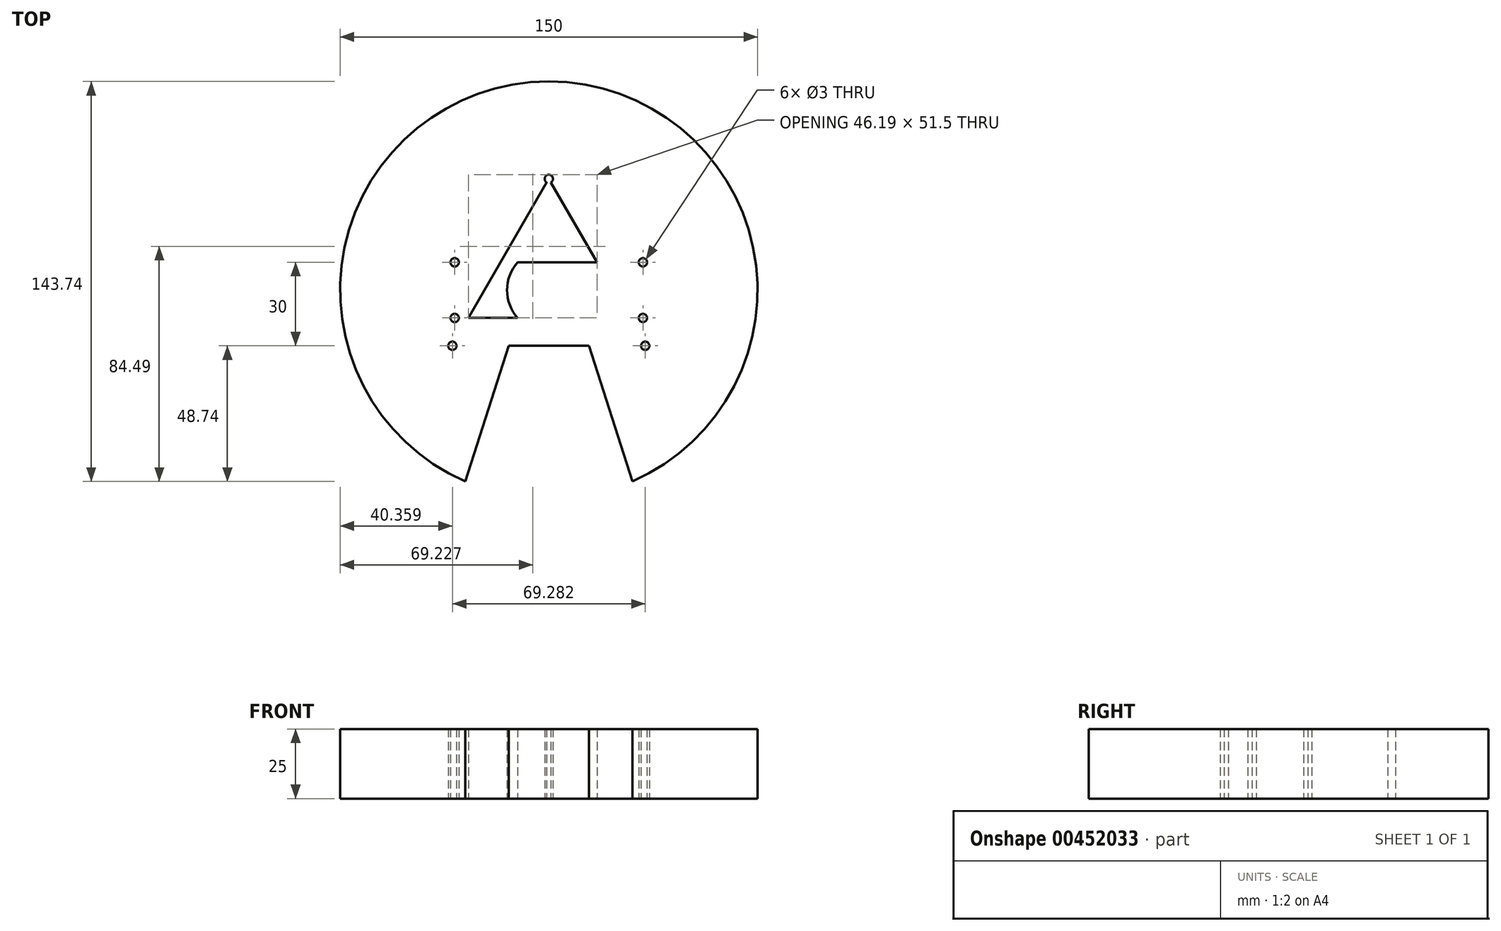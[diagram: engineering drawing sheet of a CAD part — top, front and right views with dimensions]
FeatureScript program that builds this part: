
annotation { "Feature Type Name" : "Feature", "Feature Type Description" : "" }
export const myFeature = defineFeature(function(context is Context, id is Id, definition is map)
    precondition{}
    {
        {
            var Q0;
            Q0=qCreatedBy(makeId("Top.planeOp"),FACE);
            var sketch = newSketch(context, id + "F0", { "sketchPlane" : qUnion([Q0])});
            skCircle(sketch, "E0", {"center": v(0, 0) * mm, "radius": 75 * mm});
            skCircle(sketch, "E1", {"center": v(0, 0) * mm, "radius": 15 * mm});
            skLineSegment(sketch, "E2.bottom", {"start": v(33.82, -10) * mm, "end": v(-33.82, -10) * mm});
            skLineSegment(sketch, "E2.top", {"start": v(33.82, 10) * mm, "end": v(-33.82, 10) * mm});
            skLineSegment(sketch, "E2.left", {"start": v(33.82, -10) * mm, "end": v(33.82, 10) * mm});
            skLineSegment(sketch, "E2.right", {"start": v(-33.82, -10) * mm, "end": v(-33.82, 10) * mm});
            skCircle(sketch, "E3.cCircle", {"center": v(0, 0) * mm, "radius": 20 * mm, "construction": true});
            skLineSegment(sketch, "E3.0", {"start": v(34.64, -20) * mm, "end": v(-34.64, -20) * mm});
            skLineSegment(sketch, "E3.1", {"start": v(-34.64, -20) * mm, "end": v(0, 40) * mm});
            skLineSegment(sketch, "E3.2", {"start": v(0, 40) * mm, "end": v(34.64, -20) * mm});
            skPoint(sketch, "E3.0.midPoint", {"position": v(0, -20) * mm});
            skCircle(sketch, "E4", {"center": v(0, 40) * mm, "radius": 1.5 * mm});
            skCircle(sketch, "E5", {"center": v(34.64, -20) * mm, "radius": 1.5 * mm});
            skCircle(sketch, "E6", {"center": v(-34.64, -20) * mm, "radius": 1.5 * mm});
            skCircle(sketch, "E7", {"center": v(33.82, 10) * mm, "radius": 1.5 * mm});
            skCircle(sketch, "E8", {"center": v(33.82, -10) * mm, "radius": 1.5 * mm});
            skCircle(sketch, "E9", {"center": v(-33.82, 10) * mm, "radius": 1.5 * mm});
            skCircle(sketch, "E10", {"center": v(-33.82, -10) * mm, "radius": 1.5 * mm});
            skLineSegment(sketch, "E11", {"start": v(11.18, -10) * mm, "end": v(30, -68.74) * mm});
            skLineSegment(sketch, "E12", {"start": v(-11.18, -10) * mm, "end": v(-30, -68.74) * mm});
            skSolve(sketch);
        }
        {
            var Q0;
            {var subQ3=sQuery(id+"F0.wireOp",EDGE,"E11");var subQ15=sQuery(id+"F0.wireOp",EDGE,"E0");var subQ16=makeQuery(id+"F0.imprint","INTERSECT",VERTEX,{"derivedFrom":[subQ15,subQ3]});Q0=makeQuery(id+"F0.imprint","IMPRINT",FACE,{"disambiguationData":[TD([[makeQuery(id+"F0.imprint","IMPRINT",EDGE,{"disambiguationData":[TD([[subQ16,-1.0]])],"derivedFrom":subQ15}),1.0]])]});}
            var Q1;
            {var subQ3=sQuery(id+"F0.wireOp",EDGE,"E5");var subQ5=sQuery(id+"F0.wireOp",EDGE,"E3.0");var subQ6=makeQuery(id+"F0.imprint","INTERSECT",VERTEX,{"derivedFrom":[subQ5,subQ3]});Q1=makeQuery(id+"F0.imprint","IMPRINT",FACE,{"disambiguationData":[TD([[makeQuery(id+"F0.imprint","IMPRINT",EDGE,{"disambiguationData":[TD([[subQ6,-1.0]])],"derivedFrom":subQ5}),-1.0]])]});}
            var Q2;
            {var subQ5=sQuery(id+"F0.wireOp",EDGE,"E12");var subQ7=sQuery(id+"F0.wireOp",EDGE,"E3.0");var subQ8=makeQuery(id+"F0.imprint","INTERSECT",VERTEX,{"derivedFrom":[subQ7,subQ5]});Q2=makeQuery(id+"F0.imprint","IMPRINT",FACE,{"disambiguationData":[TD([[makeQuery(id+"F0.imprint","IMPRINT",EDGE,{"disambiguationData":[TD([[subQ8,-1.0]])],"derivedFrom":subQ7}),-1.0]])]});}
            var Q3;
            {var subQ5=sQuery(id+"F0.wireOp",EDGE,"E3.1");var subQ6=sQuery(id+"F0.wireOp",EDGE,"E2.bottom");var subQ7=makeQuery(id+"F0.imprint","INTERSECT",VERTEX,{"derivedFrom":[subQ6,subQ5]});Q3=makeQuery(id+"F0.imprint","IMPRINT",FACE,{"disambiguationData":[TD([[makeQuery(id+"F0.imprint","IMPRINT",EDGE,{"disambiguationData":[TD([[subQ7,-1.0]])],"derivedFrom":subQ6}),-1.0]])]});}
            var Q4;
            {var subQ1=sQuery(id+"F0.wireOp",EDGE,"E2.top");var subQ5=sQuery(id+"F0.wireOp",EDGE,"E1");var subQ10=makeQuery(id+"F0.imprint","INTERSECT",VERTEX,{"disambiguationData":[OD(0.0)],"derivedFrom":[subQ5,subQ1]});Q4=makeQuery(id+"F0.imprint","IMPRINT",FACE,{"disambiguationData":[TD([[makeQuery(id+"F0.imprint","IMPRINT",EDGE,{"disambiguationData":[TD([[subQ10,1.0]])],"derivedFrom":subQ5}),-1.0]])]});}
            var Q5;
            {var subQ1=sQuery(id+"F0.wireOp",EDGE,"E2.bottom");var subQ5=sQuery(id+"F0.wireOp",EDGE,"E8");var subQ6=makeQuery(id+"F0.imprint","INTERSECT",VERTEX,{"derivedFrom":[subQ1,subQ5]});Q5=makeQuery(id+"F0.imprint","IMPRINT",FACE,{"disambiguationData":[TD([[makeQuery(id+"F0.imprint","IMPRINT",EDGE,{"disambiguationData":[TD([[subQ6,-1.0]])],"derivedFrom":subQ1}),-1.0]])]});}
            var Q6;
            {var subQ1=sQuery(id+"F0.wireOp",EDGE,"E1");var subQ3=sQuery(id+"F0.wireOp",EDGE,"E2.top");var subQ4=makeQuery(id+"F0.imprint","INTERSECT",VERTEX,{"disambiguationData":[OD(1.0)],"derivedFrom":[subQ1,subQ3]});Q6=makeQuery(id+"F0.imprint","IMPRINT",FACE,{"disambiguationData":[TD([[makeQuery(id+"F0.imprint","IMPRINT",EDGE,{"disambiguationData":[TD([[subQ4,1.0]])],"derivedFrom":subQ3}),1.0]])]});}
            var Q7;
            {var subQ1=sQuery(id+"F0.wireOp",EDGE,"E1");var subQ3=sQuery(id+"F0.wireOp",EDGE,"E2.top");var subQ4=makeQuery(id+"F0.imprint","INTERSECT",VERTEX,{"disambiguationData":[OD(0.0)],"derivedFrom":[subQ1,subQ3]});Q7=makeQuery(id+"F0.imprint","IMPRINT",FACE,{"disambiguationData":[TD([[makeQuery(id+"F0.imprint","IMPRINT",EDGE,{"disambiguationData":[TD([[subQ4,1.0]])],"derivedFrom":subQ3}),1.0]])]});}
            var Q8;
            {var subQ1=sQuery(id+"F0.wireOp",EDGE,"E1");var subQ3=sQuery(id+"F0.wireOp",EDGE,"E2.top");var subQ4=makeQuery(id+"F0.imprint","INTERSECT",VERTEX,{"disambiguationData":[OD(0.0)],"derivedFrom":[subQ1,subQ3]});Q8=makeQuery(id+"F0.imprint","IMPRINT",FACE,{"disambiguationData":[TD([[makeQuery(id+"F0.imprint","IMPRINT",EDGE,{"disambiguationData":[TD([[subQ4,-1.0]])],"derivedFrom":subQ3}),1.0]])]});}
            var Q9;
            {var subQ0=sQuery(id+"F0.wireOp",EDGE,"E2.top");var subQ1=sQuery(id+"F0.wireOp",EDGE,"E1");var subQ2=makeQuery(id+"F0.imprint","INTERSECT",VERTEX,{"disambiguationData":[OD(0.0)],"derivedFrom":[subQ1,subQ0]});Q9=makeQuery(id+"F0.imprint","IMPRINT",FACE,{"disambiguationData":[TD([[makeQuery(id+"F0.imprint","IMPRINT",EDGE,{"disambiguationData":[TD([[subQ2,1.0]])],"derivedFrom":subQ1}),1.0]])]});}
            var Q10;
            {var subQ0=sQuery(id+"F0.wireOp",EDGE,"E2.bottom");var subQ1=sQuery(id+"F0.wireOp",EDGE,"E1");var subQ2=makeQuery(id+"F0.imprint","INTERSECT",VERTEX,{"derivedFrom":[subQ1,subQ0,sQuery(id+"F0.wireOp",EDGE,"E11")]});Q10=makeQuery(id+"F0.imprint","IMPRINT",FACE,{"disambiguationData":[TD([[makeQuery(id+"F0.imprint","IMPRINT",EDGE,{"disambiguationData":[TD([[subQ2,1.0]])],"derivedFrom":subQ1}),1.0]])]});}
            var Q11;
            {var subQ0=sQuery(id+"F0.wireOp",EDGE,"E11");var subQ6=sQuery(id+"F0.wireOp",EDGE,"E3.0");var subQ7=makeQuery(id+"F0.imprint","INTERSECT",VERTEX,{"derivedFrom":[subQ6,subQ0]});Q11=makeQuery(id+"F0.imprint","IMPRINT",FACE,{"disambiguationData":[TD([[makeQuery(id+"F0.imprint","IMPRINT",EDGE,{"disambiguationData":[TD([[subQ7,-1.0]])],"derivedFrom":subQ6}),-1.0]])]});}
            extrude(context, id + "F1", {"entities" : qUnion([Q0, Q1, Q2, Q3, Q4, Q5, Q6, Q7, Q8, Q9, Q10, Q11]), "depth" : 25 * mm, "offsetDistance" : 25 * mm});
        }
    });
